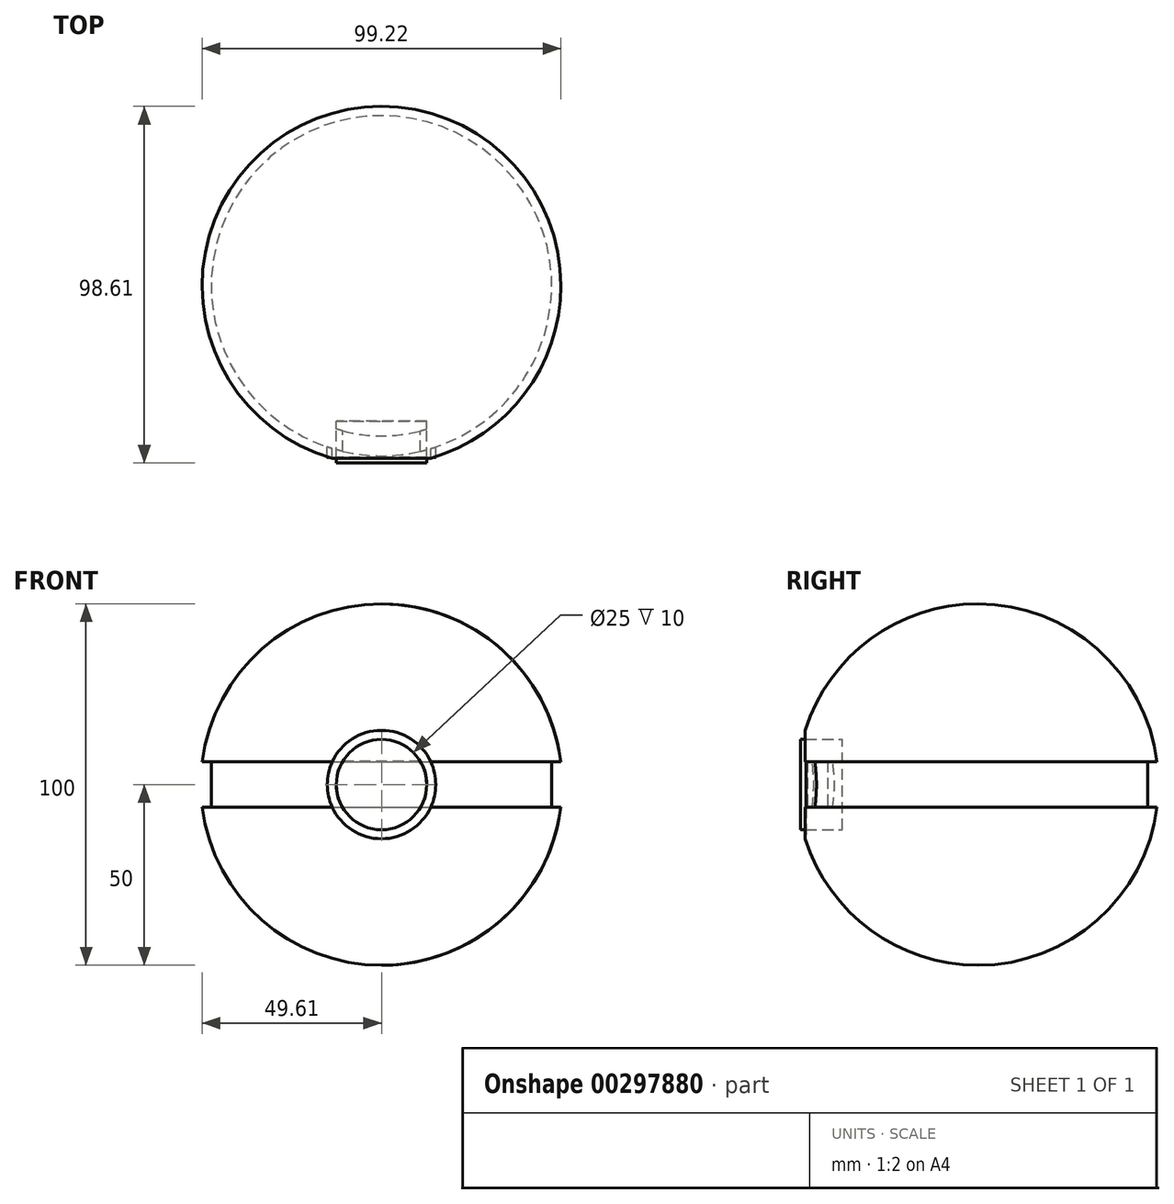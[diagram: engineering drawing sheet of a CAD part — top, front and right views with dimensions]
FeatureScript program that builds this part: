
annotation { "Feature Type Name" : "Feature", "Feature Type Description" : "" }
export const myFeature = defineFeature(function(context is Context, id is Id, definition is map)
    precondition{}
    {
        {
            var Q0;
            Q0=qCreatedBy(makeId("Top.planeOp"),FACE);
            var sketch = newSketch(context, id + "F0", { "sketchPlane" : qUnion([Q0])});
            skCircle(sketch, "E0", {"center": v(0, 0) * mm, "radius": 50 * mm});
            skSolve(sketch);
        }
        {
            var Q0;
            Q0=makeQuery(id+"F0.imprint","IMPRINT",FACE,{"disambiguationData":[TD([[makeQuery(id+"F0.imprint","IMPRINT",EDGE,{"derivedFrom":sQuery(id+"F0.wireOp",EDGE,"E0")}),1.0]])]});
            extrude(context, id + "F1", {"entities" : qUnion([Q0]), "depth" : 50 * mm});
        }
        {
            var Q0;
            Q0=makeQuery(id+"F1.opExtrude","CAP_EDGE",EDGE,{"disambiguationData":[OSD([sQuery(id+"F0.wireOp",EDGE,"E0")])],"isStart":false});
            fillet(context, id + "F2", {"entities" : qUnion([Q0]), "radius" : 50 * mm, "tangentPropagation" : true, "allowEdgeOverflow" : false});
        }
        {
            var Q0;
            Q0=makeQuery(id+"F1.opExtrude","CAP_FACE",FACE,{"disambiguationData":[OSD([sQuery(id+"F0.wireOp",EDGE,"E0")])],"isStart":true});
            extrude(context, id + "F3", {"entities" : qUnion([Q0]), "depth" : 50 * mm});
        }
        {
            var Q0;
            Q0=makeQuery(id+"F3.opExtrude","CAP_EDGE",EDGE,{"disambiguationData":[OSD([sQuery(id+"F0.wireOp",EDGE,"E0")])],"isStart":false});
            fillet(context, id + "F4", {"entities" : qUnion([Q0]), "radius" : 50 * mm, "tangentPropagation" : true, "allowEdgeOverflow" : false});
        }
        {
            var Q0;
            Q0=qCreatedBy(makeId("Front.planeOp"),FACE);
            cPlane(context, id + "F5", {"entities" : qUnion([Q0]), "cplaneType" : CPlaneType.OFFSET, "offset" : 47.5 * mm, "width" : 150 * mm, "height" : 150 * mm});
        }
        {
            var Q0;
            Q0=qCreatedBy(id+"F5.planeOp",FACE);
            var sketch = newSketch(context, id + "F6", { "sketchPlane" : qUnion([Q0])});
            skCircle(sketch, "E1", {"center": v(0, 0) * mm, "radius": 15 * mm});
            skSolve(sketch);
        }
        {
            var Q0;
            Q0 = qSketchRegion(id + "F6", true);
            extrude(context, id + "F7", {"entities" : qUnion([Q0]), "operationType" : NewBodyOperationType.REMOVE, "depth" : 2.5 * mm, "hasSecondDirection" : true, "secondDirectionOppositeDirection" : true, "secondDirectionDepth" : 10 * mm});
        }
        {
            var Q0;
            Q0=qCreatedBy(makeId("Right.planeOp"),FACE);
            var sketch = newSketch(context, id + "F8", { "sketchPlane" : qUnion([Q0])});
            skLineSegment(sketch, "E2", {"start": v(0, 0) * mm, "end": v(0, 61.06) * mm});
            skLineSegment(sketch, "E3.bottom", {"start": v(-53.66, 6.26) * mm, "end": v(-41.78, 6.26) * mm});
            skLineSegment(sketch, "E3.top", {"start": v(-53.66, -6.26) * mm, "end": v(-41.78, -6.26) * mm});
            skLineSegment(sketch, "E3.left", {"start": v(-53.66, 6.26) * mm, "end": v(-53.66, -6.26) * mm});
            skLineSegment(sketch, "E3.right", {"start": v(-41.78, 6.26) * mm, "end": v(-41.78, -6.26) * mm});
            skPoint(sketch, "E3.middle", {"position": v(-47.72, 0) * mm});
            skSolve(sketch);
        }
        {
            var Q0;
            Q0=makeQuery(id+"F8.imprint","IMPRINT",FACE,{"disambiguationData":[TD([[makeQuery(id+"F8.imprint","IMPRINT",EDGE,{"derivedFrom":sQuery(id+"F8.wireOp",EDGE,"E3.bottom")}),-1.0]])]});
            var Q1;
            Q1=sQuery(id+"F8.wireOp",EDGE,"E2");
            revolve(context, id + "F9", {"operationType" : NewBodyOperationType.REMOVE, "entities" : qUnion([Q0]), "axis" : qUnion([Q1]), "revolveType" : RevolveType.FULL, "oppositeDirection" : true});
        }
        {
            var Q0;
            Q0=qCreatedBy(makeId("Right.planeOp"),FACE);
            var sketch = newSketch(context, id + "F10", { "sketchPlane" : qUnion([Q0])});
            skLineSegment(sketch, "E4.bottom", {"start": v(41.56, 6.44) * mm, "end": v(47.06, 6.44) * mm});
            skLineSegment(sketch, "E4.top", {"start": v(41.56, -6.44) * mm, "end": v(47.06, -6.44) * mm});
            skLineSegment(sketch, "E4.left", {"start": v(41.56, 6.44) * mm, "end": v(41.56, -6.44) * mm});
            skLineSegment(sketch, "E4.right", {"start": v(47.06, 6.44) * mm, "end": v(47.06, -6.44) * mm});
            skPoint(sketch, "E4.middle", {"position": v(44.3, 0) * mm});
            skLineSegment(sketch, "E5", {"start": v(0, 0) * mm, "end": v(0, 64.8) * mm});
            skSolve(sketch);
        }
        {
            var Q0;
            Q0=makeQuery(id+"F10.imprint","IMPRINT",FACE,{"disambiguationData":[TD([[makeQuery(id+"F10.imprint","IMPRINT",EDGE,{"derivedFrom":sQuery(id+"F10.wireOp",EDGE,"E4.bottom")}),-1.0]])]});
            var Q1;
            Q1=sQuery(id+"F10.wireOp",EDGE,"E5");
            revolve(context, id + "F11", {"entities" : qUnion([Q0]), "axis" : qUnion([Q1]), "revolveType" : RevolveType.FULL});
        }
        {
            var Q0;
            {var subQ0=sQuery(id+"F6.wireOp",EDGE,"E1");Q0=makeQuery(id+"F7.boolean.opBoolean","COPY",FACE,{"disambiguationData":[TD([makeQuery(id+"F1.opExtrude","CAP_FACE",FACE,{"disambiguationData":[OSD([sQuery(id+"F0.wireOp",EDGE,"E0")])],"isStart":true})])],"derivedFrom":makeQuery(id+"F7.opExtrude","CAP_FACE",FACE,{"disambiguationData":[OSD([subQ0])],"isStart":true})});}
            var sketch = newSketch(context, id + "F12", { "sketchPlane" : qUnion([Q0])});
            skSolve(sketch);
        }
        {
            var Q0;
            {var subQ0=sQuery(id+"F6.wireOp",EDGE,"E1");var subQ1=makeQuery(id+"F7.opExtrude","CAP_FACE",FACE,{"disambiguationData":[OSD([subQ0])],"isStart":true});var subQ2=makeQuery(id+"F1.opExtrude","CAP_FACE",FACE,{"disambiguationData":[OSD([sQuery(id+"F0.wireOp",EDGE,"E0")])],"isStart":true});Q0=makeQuery(id+"F12.imprint","IMPRINT",FACE,{"disambiguationData":[TD([[makeQuery(id+"F12.imprint","IMPRINT",EDGE,{"derivedFrom":makeQuery(id+"F7.boolean.opBoolean","INTERSECT",EDGE,{"derivedFrom":[subQ2,subQ1]})}),1.0]])]});}
            var sketch = newSketch(context, id + "F13", { "sketchPlane" : qUnion([Q0])});
            skCircle(sketch, "E6", {"center": v(0, 0) * mm, "radius": 15 * mm});
            skCircle(sketch, "E7", {"center": v(0, 0) * mm, "radius": 12.5 * mm});
            skSolve(sketch);
        }
        {
            var Q0;
            Q0 = qSketchRegion(id + "F13", true);
            extrude(context, id + "F14", {"entities" : qUnion([Q0]), "operationType" : NewBodyOperationType.ADD, "depth" : 10 * mm});
        }
        {
            var Q0;
            {var subQ0=sQuery(id+"F6.wireOp",EDGE,"E1");var subQ1=makeQuery(id+"F7.opExtrude","CAP_FACE",FACE,{"disambiguationData":[OSD([subQ0])],"isStart":true});var subQ2=makeQuery(id+"F1.opExtrude","CAP_FACE",FACE,{"disambiguationData":[OSD([sQuery(id+"F0.wireOp",EDGE,"E0")])],"isStart":true});Q0=makeQuery(id+"F12.imprint","IMPRINT",FACE,{"disambiguationData":[TD([[makeQuery(id+"F12.imprint","IMPRINT",EDGE,{"derivedFrom":makeQuery(id+"F7.boolean.opBoolean","INTERSECT",EDGE,{"derivedFrom":[subQ2,subQ1]})}),1.0]])]});}
            var sketch = newSketch(context, id + "F15", { "sketchPlane" : qUnion([Q0])});
            skCircle(sketch, "E8", {"center": v(0, 0) * mm, "radius": 12.5 * mm});
            skSolve(sketch);
        }
        {
            var Q0;
            Q0 = qSketchRegion(id + "F15", true);
            extrude(context, id + "F16", {"entities" : qUnion([Q0]), "depth" : 11.5 * mm});
        }
    });
